# Revit family: Hager-IC-IP30-Plain_Door_1Row-sistema-ES-es
name_source: partatom
category: Electrical Equipment
units: mm (PartAtom-declared; Revit-internal decimal feet)

## family parameters
Cut with Voids When Loaded = No
Host = Face
Panel Configuration = Two Columns, Circuits Across
Part Type = Panelboard
Room Calculation Point = No
Round Connector Dimension = Use Diameter
Shared = No

## types (5) — shared parameters
Classification.Uniclass.Pr.Description = Control circuit device enclosures
Classification.Uniclass.Pr.Number = Pr_80_77_28_16
EF000003 - Tipo de montaje = EV000384 - Montado superficial (escayola)
EF000007 - Color = EV000202 - Blanco
EF000049 - Profundidad = 91 mm  [stored 0.298556 ft]
EF000116 - Número RAL = 9010
EF000118 - Con placa de montaje = No
EF000266 - Número de filas = 1
EF001062 - Versión de EMC = No
EF001088 - Posibilidad de extensión = Yes
EF001131 - Profundidad interna = 72 mm  [stored 0.23622 ft]
EF001134 - Carril DIN = Yes
EF001596 - Material de la carcasa = EV000139 - Plástico
EF004462 - Tipo de cierre = EV000154 - Otros
EF005474 - Grado de protección (IP) = EV006410 - IP30
EF006244 - Tapa/puerta transparente = No
EF006306 - Con cierre = No
EF009212 - Versión de la cubierta = EV000116 - Cerrado
EF015776 - Borne de tierra = No
EF015777 - Borne neutro = No
EF015941 - Puerta de transmisión de señal = Yes
Ground Bus = No
HG000002 - Con puerta o tapa = Yes
HG000003 - Gama = IC
HG000005 - Grosor = 3 mm  [stored 0.00984252 ft]
HG000006 - Empotrado = No
HG000017 - Distancia entre polos = 18 mm  [stored 0.0590551 ft]
Manufacturer = Hager
Neutral Bus = No
Type Comments = IC
zero-valued in all types: Default Elevation, EF000218 - Profundidad de instalación, EF000332 - Altura de la instalación, EF000846 - Anchura de instalación

## per-type parameters (varying)
| type | EF000008 - Anchura | EF000040 - Altura | EF002950 - Anchura de unidades de división | HG000004 - Referencia del fabricante | Model |
| Montado superficial IP30 A134.5 A170 P91 6 unidad de división - VD106NE | 134 mm | 170 mm  [stored 0.557743 ft] | 6 | VD106NE | VD106NE |
| Montado superficial IP30 A170.5 A170 P91 8 unidad de división - VD108NE | 170 mm  [stored 0.557743 ft] | 170 mm  [stored 0.557743 ft] | 8 | VD108NE | VD108NE |
| Montado superficial IP30 A206.5 A170 P91 10 unidad de división - VD110NE | 206 mm  [stored 0.675853 ft] | 170 mm  [stored 0.557743 ft] | 10 | VD110NE | VD110NE |
| Montado superficial IP30 A292.5 A200 P91 12 unidad de división - VD112NE | 292 mm  [stored 0.958005 ft] | 200 mm  [stored 0.656168 ft] | 12 | VD112NE | VD112NE |
| Montado superficial IP30 A400 A200 P91 18 unidad de división - VD118NE | 400 mm  [stored 1.31234 ft] | 200 mm  [stored 0.656168 ft] | 18 | VD118NE | VD118NE |

note: [stored X ft] marks values corroborated as IEEE doubles in the binary element streams (Revit-internal decimal feet)

## geometry (parser evidence)
native form markers: Blend x4, Sweep x12
no freeform markers — native parametric forms only
